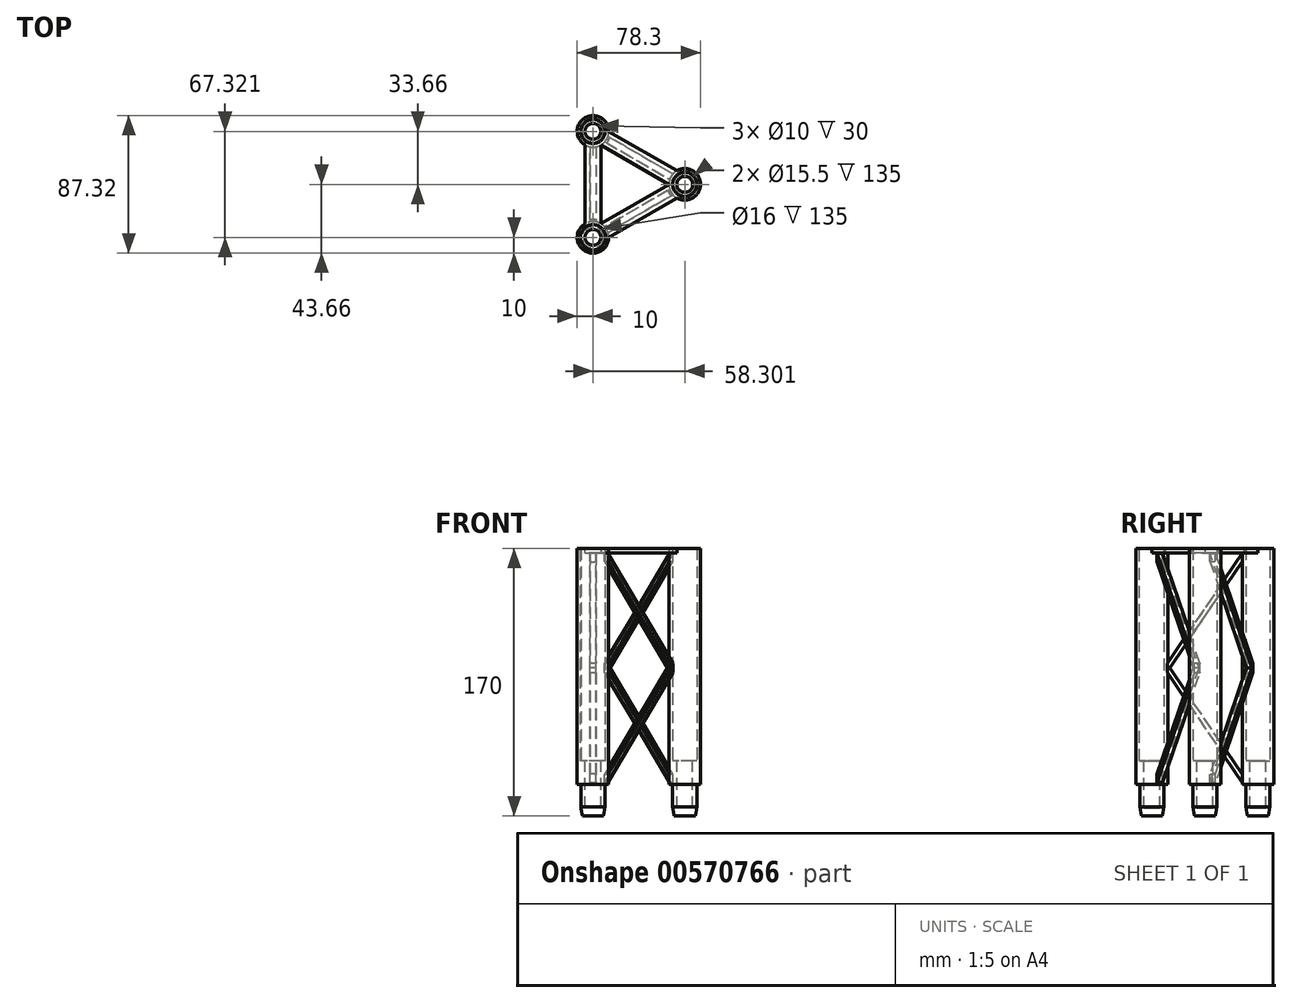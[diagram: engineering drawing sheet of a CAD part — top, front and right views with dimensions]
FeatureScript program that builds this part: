
annotation { "Feature Type Name" : "Feature", "Feature Type Description" : "" }
export const myFeature = defineFeature(function(context is Context, id is Id, definition is map)
    precondition{}
    {
        {
            var Q0;
            Q0=qCreatedBy(makeId("Top.planeOp"),FACE);
            var sketch = newSketch(context, id + "F0", { "sketchPlane" : qUnion([Q0])});
            skLineSegment(sketch, "E0", {"start": v(0, 0) * mm, "end": v(0, -50) * mm});
            skLineSegment(sketch, "E1", {"start": v(0, -50) * mm, "end": v(43.3, -25) * mm});
            skLineSegment(sketch, "E2", {"start": v(43.3, -25) * mm, "end": v(0, 0) * mm});
            skLineSegment(sketch, "E3", {"start": v(-10, 17.32) * mm, "end": v(-10, -67.32) * mm});
            skLineSegment(sketch, "E4", {"start": v(-10, -67.32) * mm, "end": v(63.3, -25) * mm});
            skLineSegment(sketch, "E5", {"start": v(63.3, -25) * mm, "end": v(-10, 17.32) * mm});
            skSolve(sketch);
        }
        {
            var Q0;
            Q0 = qSketchRegion(id + "F0", true);
            extrude(context, id + "F1", {"entities" : qUnion([Q0]), "depth" : 3 * mm, "offsetDistance" : 25 * mm});
        }
        {
            var Q0;
            Q0=makeQuery(id+"F1.opExtrude","CAP_FACE",FACE,{"disambiguationData":[OSD([sQuery(id+"F0.wireOp",EDGE,"E0"),sQuery(id+"F0.wireOp",EDGE,"E1"),sQuery(id+"F0.wireOp",EDGE,"E2"),sQuery(id+"F0.wireOp",EDGE,"E3"),sQuery(id+"F0.wireOp",EDGE,"E4"),sQuery(id+"F0.wireOp",EDGE,"E5")])],"isStart":false});
            var sketch = newSketch(context, id + "F2", { "sketchPlane" : qUnion([Q0])});
            skCircle(sketch, "E6", {"center": v(-5, 8.66) * mm, "radius": 10 * mm});
            skCircle(sketch, "E7", {"center": v(53.3, -25) * mm, "radius": 10 * mm});
            skCircle(sketch, "E8", {"center": v(-5, -58.66) * mm, "radius": 10 * mm});
            skSolve(sketch);
        }
        {
            var Q0;
            Q0 = qSketchRegion(id + "F2", true);
            extrude(context, id + "F3", {"entities" : qUnion([Q0]), "operationType" : NewBodyOperationType.ADD, "oppositeDirection" : true, "depth" : 150 * mm, "offsetDistance" : 25 * mm});
        }
        {
            var Q0;
            {var subQ0=sQuery(id+"F0.wireOp",EDGE,"E2");var subQ1=sQuery(id+"F0.wireOp",EDGE,"E1");var subQ2=sQuery(id+"F0.wireOp",EDGE,"E3");var subQ3=sQuery(id+"F0.wireOp",EDGE,"E0");var subQ4=makeQuery(id+"F1.opExtrude","CAP_FACE",FACE,{"disambiguationData":[OSD([subQ3,subQ1,subQ0,subQ2,sQuery(id+"F0.wireOp",EDGE,"E4"),sQuery(id+"F0.wireOp",EDGE,"E5")])],"isStart":true});Q0=makeQuery(id+"F3.boolean.opBoolean","SPLIT",FACE,{"disambiguationData":[TD([makeQuery(id+"F1.opExtrude","SWEPT_FACE",FACE,{"disambiguationData":[OSD([subQ2])]})])],"derivedFrom":subQ4});}
            var sketch = newSketch(context, id + "F4", { "sketchPlane" : qUnion([Q0])});
            skLineSegment(sketch, "E9.bottom", {"start": v(-3, 48.86) * mm, "end": v(-7, 48.86) * mm});
            skLineSegment(sketch, "E9.top", {"start": v(-3, 1.14) * mm, "end": v(-7, 1.14) * mm});
            skLineSegment(sketch, "E10.bottom", {"start": v(-7, 48.86) * mm, "end": v(-3, 48.86) * mm});
            skLineSegment(sketch, "E10.top", {"start": v(-7, 1.14) * mm, "end": v(-3, 1.14) * mm});
            skLineSegment(sketch, "E10.left", {"start": v(-7, 48.86) * mm, "end": v(-7, 1.14) * mm});
            skLineSegment(sketch, "E10.right", {"start": v(-3, 48.86) * mm, "end": v(-3, 1.14) * mm});
            skSolve(sketch);
        }
        {
            var Q0;
            Q0 = qSketchRegion(id + "F4", true);
            extrude(context, id + "F5", {"entities" : qUnion([Q0]), "operationType" : NewBodyOperationType.ADD, "depth" : 146 * mm, "offsetDistance" : 25 * mm});
        }
        {
            var Q0;
            {var subQ0=sQuery(id+"F0.wireOp",EDGE,"E2");var subQ1=sQuery(id+"F0.wireOp",EDGE,"E1");var subQ2=sQuery(id+"F0.wireOp",EDGE,"E5");var subQ3=sQuery(id+"F0.wireOp",EDGE,"E0");var subQ4=makeQuery(id+"F1.opExtrude","CAP_FACE",FACE,{"disambiguationData":[OSD([subQ3,subQ1,subQ0,sQuery(id+"F0.wireOp",EDGE,"E3"),sQuery(id+"F0.wireOp",EDGE,"E4"),subQ2])],"isStart":true});Q0=makeQuery(id+"F3.boolean.opBoolean","SPLIT",FACE,{"disambiguationData":[TD([makeQuery(id+"F1.opExtrude","SWEPT_FACE",FACE,{"disambiguationData":[OSD([subQ2])]})])],"derivedFrom":subQ4});}
            var sketch = newSketch(context, id + "F6", { "sketchPlane" : qUnion([Q0])});
            skLineSegment(sketch, "E11.right", {"start": v(45.82, 18.37) * mm, "end": v(43.82, 21.83) * mm});
            skLineSegment(sketch, "E12", {"start": v(45.82, 18.37) * mm, "end": v(4.49, -5.5) * mm});
            skLineSegment(sketch, "E13", {"start": v(43.82, 21.83) * mm, "end": v(2.49, -2.03) * mm});
            skPoint(sketch, "E11.top.start.orphan", {"position": v(0, 0) * mm});
            skLineSegment(sketch, "E14", {"start": v(4.49, -5.5) * mm, "end": v(2.49, -2.03) * mm});
            skSolve(sketch);
        }
        {
            var Q0;
            Q0 = qSketchRegion(id + "F6", true);
            extrude(context, id + "F7", {"entities" : qUnion([Q0]), "operationType" : NewBodyOperationType.ADD, "depth" : 146 * mm, "offsetDistance" : 25 * mm});
        }
        {
            var Q0;
            {var subQ0=sQuery(id+"F0.wireOp",EDGE,"E2");var subQ1=sQuery(id+"F0.wireOp",EDGE,"E1");var subQ2=sQuery(id+"F0.wireOp",EDGE,"E4");var subQ3=sQuery(id+"F0.wireOp",EDGE,"E0");var subQ4=makeQuery(id+"F1.opExtrude","CAP_FACE",FACE,{"disambiguationData":[OSD([subQ3,subQ1,subQ0,sQuery(id+"F0.wireOp",EDGE,"E3"),subQ2,sQuery(id+"F0.wireOp",EDGE,"E5")])],"isStart":true});Q0=makeQuery(id+"F3.boolean.opBoolean","SPLIT",FACE,{"disambiguationData":[TD([makeQuery(id+"F1.opExtrude","SWEPT_FACE",FACE,{"disambiguationData":[OSD([subQ2])]})])],"derivedFrom":subQ4});}
            var sketch = newSketch(context, id + "F8", { "sketchPlane" : qUnion([Q0])});
            skLineSegment(sketch, "E15", {"start": v(45.82, 31.63) * mm, "end": v(4.49, 55.5) * mm});
            skLineSegment(sketch, "E16", {"start": v(4.49, 55.5) * mm, "end": v(2.49, 52.03) * mm});
            skLineSegment(sketch, "E17", {"start": v(2.49, 52.03) * mm, "end": v(43.82, 28.17) * mm});
            skLineSegment(sketch, "E18", {"start": v(43.82, 28.17) * mm, "end": v(45.82, 31.63) * mm});
            skSolve(sketch);
        }
        {
            var Q0;
            Q0 = qSketchRegion(id + "F8", true);
            extrude(context, id + "F9", {"entities" : qUnion([Q0]), "operationType" : NewBodyOperationType.ADD, "depth" : 146 * mm, "offsetDistance" : 25 * mm});
        }
        {
            var Q0;
            Q0=makeQuery(id+"F5.opExtrude","SWEPT_FACE",FACE,{"disambiguationData":[OSD([sQuery(id+"F4.wireOp",EDGE,"E10.left")])]});
            var sketch = newSketch(context, id + "F10", { "sketchPlane" : qUnion([Q0])});
            skLineSegment(sketch, "E19", {"start": v(1.14, -146) * mm, "end": v(48.86, -146) * mm});
            skLineSegment(sketch, "E20", {"start": v(48.86, -146) * mm, "end": v(48.86, -76) * mm});
            skLineSegment(sketch, "E21", {"start": v(48.86, -76) * mm, "end": v(1.14, -146) * mm});
            skLineSegment(sketch, "E22", {"start": v(48.86, 0) * mm, "end": v(1.14, 0) * mm});
            skLineSegment(sketch, "E23", {"start": v(1.14, 0) * mm, "end": v(48.86, -70) * mm});
            skLineSegment(sketch, "E24", {"start": v(48.86, -70) * mm, "end": v(48.86, 0) * mm});
            skLineSegment(sketch, "E25", {"start": v(1.14, -140.67) * mm, "end": v(47.28, -73) * mm});
            skLineSegment(sketch, "E26", {"start": v(47.28, -73) * mm, "end": v(1.14, -5.33) * mm});
            skLineSegment(sketch, "E27", {"start": v(1.14, -5.33) * mm, "end": v(1.14, -140.67) * mm});
            skSolve(sketch);
        }
        {
            var Q0;
            Q0 = qSketchRegion(id + "F10", true);
            extrude(context, id + "F11", {"entities" : qUnion([Q0]), "operationType" : NewBodyOperationType.REMOVE, "endBound" : BoundingType.UP_TO_NEXT, "oppositeDirection" : true, "depth" : 25 * mm, "offsetDistance" : 25 * mm});
        }
        {
            var Q0;
            Q0=makeQuery(id+"F7.opExtrude","SWEPT_FACE",FACE,{"disambiguationData":[OSD([sQuery(id+"F6.wireOp",EDGE,"E12")])]});
            var sketch = newSketch(context, id + "F12", { "sketchPlane" : qUnion([Q0])});
            skLineSegment(sketch, "E28", {"start": v(-48.86, -146) * mm, "end": v(-1.14, -146) * mm});
            skLineSegment(sketch, "E29", {"start": v(-1.14, -146) * mm, "end": v(-1.14, -76) * mm});
            skLineSegment(sketch, "E30", {"start": v(-1.14, -76) * mm, "end": v(-48.86, -146) * mm});
            skLineSegment(sketch, "E31", {"start": v(-1.14, 0) * mm, "end": v(-48.86, 0) * mm});
            skLineSegment(sketch, "E32", {"start": v(-48.86, 0) * mm, "end": v(-1.14, -70) * mm});
            skLineSegment(sketch, "E33", {"start": v(-1.14, -70) * mm, "end": v(-1.14, 0) * mm});
            skLineSegment(sketch, "E34", {"start": v(-48.86, -140.67) * mm, "end": v(-2.72, -73) * mm});
            skLineSegment(sketch, "E35", {"start": v(-2.72, -73) * mm, "end": v(-48.86, -5.33) * mm});
            skLineSegment(sketch, "E36", {"start": v(-48.86, -5.33) * mm, "end": v(-48.86, -140.67) * mm});
            skSolve(sketch);
        }
        {
            var Q0;
            Q0 = qSketchRegion(id + "F12", true);
            extrude(context, id + "F13", {"entities" : qUnion([Q0]), "operationType" : NewBodyOperationType.REMOVE, "endBound" : BoundingType.UP_TO_NEXT, "oppositeDirection" : true, "depth" : 25 * mm, "offsetDistance" : 25 * mm});
        }
        {
            var Q0;
            Q0=makeQuery(id+"F9.opExtrude","SWEPT_FACE",FACE,{"disambiguationData":[OSD([sQuery(id+"F8.wireOp",EDGE,"E15")])]});
            var sketch = newSketch(context, id + "F14", { "sketchPlane" : qUnion([Q0])});
            skLineSegment(sketch, "E37", {"start": v(-23.86, -146) * mm, "end": v(23.86, -146) * mm});
            skLineSegment(sketch, "E38", {"start": v(23.86, -146) * mm, "end": v(23.86, -76) * mm});
            skLineSegment(sketch, "E39", {"start": v(23.86, -76) * mm, "end": v(-23.86, -146) * mm});
            skLineSegment(sketch, "E40", {"start": v(23.86, 0) * mm, "end": v(-23.86, 0) * mm});
            skLineSegment(sketch, "E41", {"start": v(-23.86, 0) * mm, "end": v(23.86, -70) * mm});
            skLineSegment(sketch, "E42", {"start": v(23.86, -70) * mm, "end": v(23.86, 0) * mm});
            skLineSegment(sketch, "E43", {"start": v(-23.86, -140.67) * mm, "end": v(22.28, -73) * mm});
            skLineSegment(sketch, "E44", {"start": v(22.28, -73) * mm, "end": v(-23.86, -5.33) * mm});
            skLineSegment(sketch, "E45", {"start": v(-23.86, -5.33) * mm, "end": v(-23.86, -140.67) * mm});
            skSolve(sketch);
        }
        {
            var Q0;
            Q0 = qSketchRegion(id + "F14", true);
            extrude(context, id + "F15", {"entities" : qUnion([Q0]), "operationType" : NewBodyOperationType.REMOVE, "endBound" : BoundingType.UP_TO_NEXT, "oppositeDirection" : true, "depth" : 25 * mm, "offsetDistance" : 25 * mm});
        }
        {
            var Q0;
            {var subQ0=sQuery(id+"F2.wireOp",EDGE,"E8");var subQ1=makeQuery(id+"F3.opExtrude","SWEPT_FACE",FACE,{"disambiguationData":[OSD([subQ0])]});var subQ2=sQuery(id+"F8.wireOp",EDGE,"yp5aDsaY-B9PL-FNCT-Ewmp-3slFSpvjve5o");var subQ4=sQuery(id+"F8.wireOp",EDGE,"jMsbRxWJ-DfRl-EBQu-Eoui-9Uk2O0zzfBLr");var subQ5=sQuery(id+"F2.wireOp",EDGE,"E6");var subQ6=sQuery(id+"F4.wireOp",EDGE,"E9.right");var subQ7=sQuery(id+"F4.wireOp",EDGE,"E9.left");var subQ8=sQuery(id+"F6.wireOp",EDGE,"E11.top");var subQ9=sQuery(id+"F6.wireOp",EDGE,"E11.bottom");var subQ10=sQuery(id+"F2.wireOp",EDGE,"E7");var subQ11=makeQuery(id+"F7.boolean.opBoolean","MERGE",FACE,{"derivedFrom":[makeQuery(id+"F3.opExtrude","CAP_FACE",FACE,{"disambiguationData":[OSD([subQ10])],"isStart":false}),makeQuery(id+"F5.boolean.opBoolean","MERGE",FACE,{"derivedFrom":[makeQuery(id+"F3.opExtrude","CAP_FACE",FACE,{"disambiguationData":[OSD([subQ5])],"isStart":false}),makeQuery(id+"F3.opExtrude","CAP_FACE",FACE,{"disambiguationData":[OSD([subQ0])],"isStart":false}),makeQuery(id+"F5.opExtrude","CAP_FACE",FACE,{"disambiguationData":[OSD([sQuery(id+"F4.wireOp",EDGE,"E9.bottom"),sQuery(id+"F4.wireOp",EDGE,"E9.top"),subQ7,subQ6])],"isStart":false})]}),makeQuery(id+"F7.opExtrude","CAP_FACE",FACE,{"disambiguationData":[OSD([subQ9,subQ8,sQuery(id+"F6.wireOp",EDGE,"E11.left"),sQuery(id+"F6.wireOp",EDGE,"E11.right")])],"isStart":false})]});Q0=makeQuery(id+"FTBP6PZqmaUpsQT_1.boolean.opBoolean","SPLIT",FACE,{"disambiguationData":[TD([makeQuery(id+"F1.opExtrude","SWEPT_FACE",FACE,{"disambiguationData":[OSD([sQuery(id+"F0.wireOp",EDGE,"E1")])]})])],"derivedFrom":makeQuery(id+"F9.boolean.opBoolean","MERGE",FACE,{"derivedFrom":[makeQuery(id+"FtjCsMNisg086rA_1.boolean.opBoolean","SPLIT",FACE,{"disambiguationData":[TD([makeQuery(id+"F1.opExtrude","SWEPT_FACE",FACE,{"disambiguationData":[OSD([sQuery(id+"F0.wireOp",EDGE,"E2")])]})])],"derivedFrom":subQ11}),makeQuery(id+"FoQTNlv1W2yDtDU_1.boolean.opBoolean","SPLIT",FACE,{"disambiguationData":[TD([subQ1])],"derivedFrom":makeQuery(id+"FtjCsMNisg086rA_1.boolean.opBoolean","SPLIT",FACE,{"disambiguationData":[TD([makeQuery(id+"F1.opExtrude","SWEPT_FACE",FACE,{"disambiguationData":[OSD([sQuery(id+"F0.wireOp",EDGE,"E0")])]})])],"derivedFrom":subQ11})}),makeQuery(id+"F9.opExtrude","CAP_FACE",FACE,{"disambiguationData":[OSD([sQuery(id+"F8.wireOp",EDGE,"3hsvIb1v-xkrR-7TYB-6jII-v0jS53BqxYlD"),subQ2,sQuery(id+"F8.wireOp",EDGE,"buLR25Rd-8MFC-uq7l-KHPV-R0JZtzQe3wKI"),subQ4])],"isStart":false})]})});}
            var sketch = newSketch(context, id + "F16", { "sketchPlane" : qUnion([Q0])});
            skCircle(sketch, "E46", {"center": v(-5, 58.66) * mm, "radius": 10 * mm});
            skSolve(sketch);
        }
        {
            var Q0;
            Q0 = qSketchRegion(id + "F16", true);
            extrude(context, id + "F17", {"entities" : qUnion([Q0]), "operationType" : NewBodyOperationType.ADD, "oppositeDirection" : true, "depth" : 150 * mm, "offsetDistance" : 25 * mm});
        }
        {
            var Q0;
            Q0=makeQuery(id+"F3.boolean.opBoolean","MERGE",FACE,{"derivedFrom":[makeQuery(id+"F1.opExtrude","CAP_FACE",FACE,{"disambiguationData":[OSD([sQuery(id+"F0.wireOp",EDGE,"E0"),sQuery(id+"F0.wireOp",EDGE,"E1"),sQuery(id+"F0.wireOp",EDGE,"E2"),sQuery(id+"F0.wireOp",EDGE,"E3"),sQuery(id+"F0.wireOp",EDGE,"E4"),sQuery(id+"F0.wireOp",EDGE,"E5")])],"isStart":false}),makeQuery(id+"F3.opExtrude","CAP_FACE",FACE,{"disambiguationData":[OSD([sQuery(id+"F2.wireOp",EDGE,"E6")])],"isStart":true}),makeQuery(id+"F3.opExtrude","CAP_FACE",FACE,{"disambiguationData":[OSD([sQuery(id+"F2.wireOp",EDGE,"E7")])],"isStart":true}),makeQuery(id+"F3.opExtrude","CAP_FACE",FACE,{"disambiguationData":[OSD([sQuery(id+"F2.wireOp",EDGE,"E8")])],"isStart":true})]});
            var sketch = newSketch(context, id + "F18", { "sketchPlane" : qUnion([Q0])});
            skCircle(sketch, "E47", {"center": v(-5, 8.66) * mm, "radius": 8 * mm});
            skCircle(sketch, "E48", {"center": v(53.3, -25) * mm, "radius": 8 * mm});
            skCircle(sketch, "E49", {"center": v(-5, -58.66) * mm, "radius": 8 * mm});
            skSolve(sketch);
        }
        {
            var Q0;
            Q0 = qSketchRegion(id + "F18", true);
            extrude(context, id + "F19", {"entities" : qUnion([Q0]), "operationType" : NewBodyOperationType.REMOVE, "oppositeDirection" : true, "depth" : 135 * mm, "offsetDistance" : 25 * mm});
        }
        {
            var Q0;
            Q0=makeQuery(id+"F3.opExtrude","CAP_FACE",FACE,{"disambiguationData":[OSD([sQuery(id+"F2.wireOp",EDGE,"E8")])],"isStart":false});
            var sketch = newSketch(context, id + "F20", { "sketchPlane" : qUnion([Q0])});
            skCircle(sketch, "E50", {"center": v(-5, 58.66) * mm, "radius": 7.75 * mm});
            skSolve(sketch);
        }
        {
            var Q0;
            Q0 = qSketchRegion(id + "F20", true);
            extrude(context, id + "F21", {"entities" : qUnion([Q0]), "operationType" : NewBodyOperationType.ADD, "depth" : 20 * mm, "offsetDistance" : 25 * mm});
        }
        {
            var Q0;
            Q0=makeQuery(id+"F21.opExtrude","CAP_EDGE",EDGE,{"disambiguationData":[OSD([sQuery(id+"F20.wireOp",EDGE,"E50")])],"isStart":false});
            chamfer(context, id + "F22", {"entities" : qUnion([Q0]), "chamferType" : ChamferType.OFFSET_ANGLE, "width" : 1 * mm, "oppositeDirection" : false, "angle" : 80 * degree, "tangentPropagation" : true});
        }
        {
            var Q0;
            Q0=makeQuery(id+"F19.boolean.opBoolean","COPY",FACE,{"derivedFrom":makeQuery(id+"F19.opExtrude","CAP_FACE",FACE,{"disambiguationData":[OSD([sQuery(id+"F18.wireOp",EDGE,"E49")])],"isStart":false})});
            var sketch = newSketch(context, id + "F23", { "sketchPlane" : qUnion([Q0])});
            skCircle(sketch, "E51", {"center": v(-5, -58.66) * mm, "radius": 5 * mm});
            skSolve(sketch);
        }
        {
            var Q0;
            Q0 = qSketchRegion(id + "F23", true);
            extrude(context, id + "F24", {"entities" : qUnion([Q0]), "operationType" : NewBodyOperationType.REMOVE, "oppositeDirection" : true, "depth" : 30 * mm, "offsetDistance" : 25 * mm});
        }
        {
            var Q0;
            Q0=makeQuery(id+"F3.opExtrude","CAP_FACE",FACE,{"disambiguationData":[OSD([sQuery(id+"F2.wireOp",EDGE,"E7")])],"isStart":false});
            var sketch = newSketch(context, id + "F25", { "sketchPlane" : qUnion([Q0])});
            skCircle(sketch, "E52", {"center": v(53.3, 25) * mm, "radius": 7.75 * mm});
            skSolve(sketch);
        }
        {
            var Q0;
            Q0 = qSketchRegion(id + "F25", true);
            extrude(context, id + "F26", {"entities" : qUnion([Q0]), "operationType" : NewBodyOperationType.ADD, "depth" : 20 * mm, "offsetDistance" : 25 * mm});
        }
        {
            var Q0;
            Q0=makeQuery(id+"F26.opExtrude","CAP_EDGE",EDGE,{"disambiguationData":[OSD([sQuery(id+"F25.wireOp",EDGE,"E52")])],"isStart":false});
            chamfer(context, id + "F27", {"entities" : qUnion([Q0]), "chamferType" : ChamferType.OFFSET_ANGLE, "width" : 1 * mm, "oppositeDirection" : false, "angle" : 80 * degree, "tangentPropagation" : true});
        }
        {
            var Q0;
            Q0=makeQuery(id+"F19.boolean.opBoolean","COPY",FACE,{"derivedFrom":makeQuery(id+"F19.opExtrude","CAP_FACE",FACE,{"disambiguationData":[OSD([sQuery(id+"F18.wireOp",EDGE,"E48")])],"isStart":false})});
            var sketch = newSketch(context, id + "F28", { "sketchPlane" : qUnion([Q0])});
            skCircle(sketch, "E53", {"center": v(53.3, -25) * mm, "radius": 5 * mm});
            skSolve(sketch);
        }
        {
            var Q0;
            Q0 = qSketchRegion(id + "F28", true);
            extrude(context, id + "F29", {"entities" : qUnion([Q0]), "operationType" : NewBodyOperationType.REMOVE, "oppositeDirection" : true, "depth" : 30 * mm, "offsetDistance" : 25 * mm});
        }
        {
            var Q0;
            Q0=makeQuery(id+"F3.opExtrude","CAP_FACE",FACE,{"disambiguationData":[OSD([sQuery(id+"F2.wireOp",EDGE,"E6")])],"isStart":false});
            var sketch = newSketch(context, id + "F30", { "sketchPlane" : qUnion([Q0])});
            skCircle(sketch, "E54", {"center": v(-5, -8.66) * mm, "radius": 7.75 * mm});
            skSolve(sketch);
        }
        {
            var Q0;
            Q0 = qSketchRegion(id + "F30", true);
            extrude(context, id + "F31", {"entities" : qUnion([Q0]), "operationType" : NewBodyOperationType.ADD, "depth" : 20 * mm, "offsetDistance" : 25 * mm});
        }
        {
            var Q0;
            Q0=makeQuery(id+"F31.opExtrude","CAP_EDGE",EDGE,{"disambiguationData":[OSD([sQuery(id+"F30.wireOp",EDGE,"E54")])],"isStart":false});
            chamfer(context, id + "F32", {"entities" : qUnion([Q0]), "chamferType" : ChamferType.OFFSET_ANGLE, "width" : 1 * mm, "oppositeDirection" : false, "angle" : 80 * degree, "tangentPropagation" : true});
        }
        {
            var Q0;
            Q0=makeQuery(id+"F19.boolean.opBoolean","COPY",FACE,{"derivedFrom":makeQuery(id+"F19.opExtrude","CAP_FACE",FACE,{"disambiguationData":[OSD([sQuery(id+"F18.wireOp",EDGE,"E47")])],"isStart":false})});
            var sketch = newSketch(context, id + "F33", { "sketchPlane" : qUnion([Q0])});
            skCircle(sketch, "E55", {"center": v(-5, 8.66) * mm, "radius": 5 * mm});
            skSolve(sketch);
        }
        {
            var Q0;
            Q0 = qSketchRegion(id + "F33", true);
            extrude(context, id + "F34", {"entities" : qUnion([Q0]), "operationType" : NewBodyOperationType.REMOVE, "oppositeDirection" : true, "depth" : 30 * mm, "offsetDistance" : 25 * mm});
        }
        {
            var Q0;
            Q0=makeQuery(id+"F3.opExtrude","CAP_FACE",FACE,{"disambiguationData":[OSD([sQuery(id+"F2.wireOp",EDGE,"E6")])],"isStart":false});
            var sketch = newSketch(context, id + "F35", { "sketchPlane" : qUnion([Q0])});
            skCircle(sketch, "E56", {"center": v(-5, -8.66) * mm, "radius": 10 * mm});
            skCircle(sketch, "E57", {"center": v(-5, -8.66) * mm, "radius": 7.75 * mm});
            skSolve(sketch);
        }
        {
            var Q0;
            Q0 = qSketchRegion(id + "F35", true);
            extrude(context, id + "F36", {"entities" : qUnion([Q0]), "operationType" : NewBodyOperationType.ADD, "oppositeDirection" : true, "depth" : 150 * mm, "offsetDistance" : 25 * mm});
        }
        {
            var Q0;
            Q0=makeQuery(id+"F3.opExtrude","CAP_FACE",FACE,{"disambiguationData":[OSD([sQuery(id+"F2.wireOp",EDGE,"E7")])],"isStart":false});
            var sketch = newSketch(context, id + "F37", { "sketchPlane" : qUnion([Q0])});
            skCircle(sketch, "E58", {"center": v(53.3, 25) * mm, "radius": 10 * mm});
            skCircle(sketch, "E59", {"center": v(53.3, 25) * mm, "radius": 7.75 * mm});
            skSolve(sketch);
        }
        {
            var Q0;
            Q0 = qSketchRegion(id + "F37", true);
            extrude(context, id + "F38", {"entities" : qUnion([Q0]), "operationType" : NewBodyOperationType.ADD, "oppositeDirection" : true, "depth" : 150 * mm, "offsetDistance" : 25 * mm});
        }
    });
